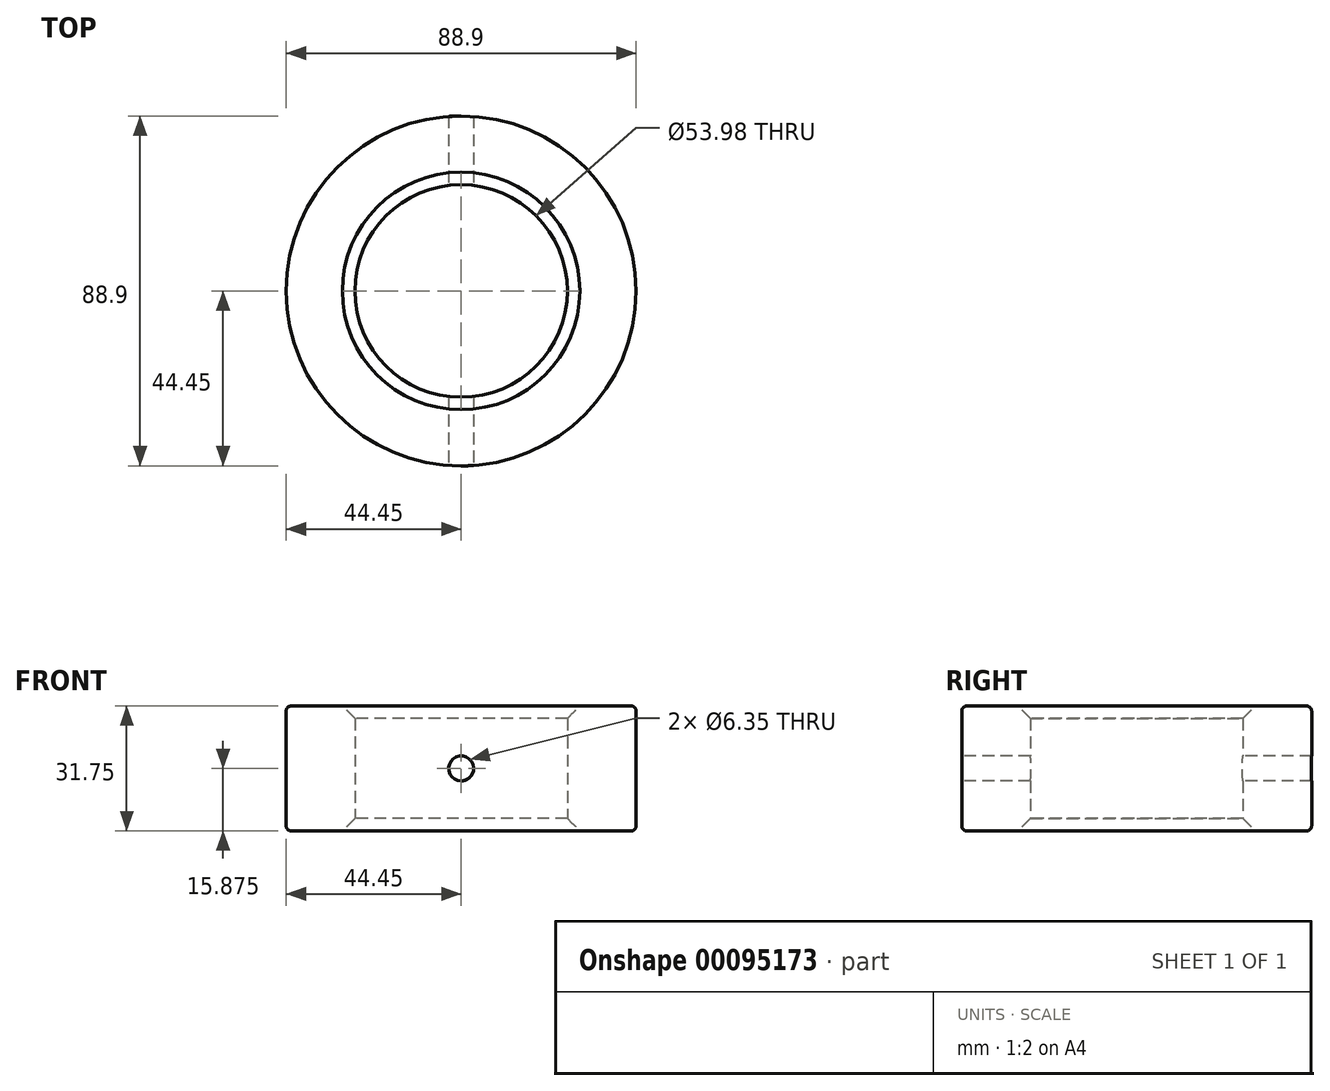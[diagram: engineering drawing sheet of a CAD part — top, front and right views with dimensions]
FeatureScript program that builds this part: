
annotation { "Feature Type Name" : "Feature", "Feature Type Description" : "" }
export const myFeature = defineFeature(function(context is Context, id is Id, definition is map)
    precondition{}
    {
        {
            var Q0;
            Q0=qCreatedBy(makeId("Top.planeOp"),FACE);
            var sketch = newSketch(context, id + "F0", { "sketchPlane" : qUnion([Q0])});
            skCircle(sketch, "E0", {"center": v(0, 0) * mm, "radius": 44.45 * mm});
            skCircle(sketch, "E1", {"center": v(0, 0) * mm, "radius": 26.99 * mm});
            skSolve(sketch);
        }
        {
            var Q0;
            Q0=makeQuery(id+"F0.imprint","IMPRINT",FACE,{"disambiguationData":[TD([[makeQuery(id+"F0.imprint","IMPRINT",EDGE,{"derivedFrom":sQuery(id+"F0.wireOp",EDGE,"E0")}),1.0]])]});
            extrude(context, id + "F1", {"entities" : qUnion([Q0]), "depth" : 31.75 * mm});
        }
        {
            var Q0;
            Q0=qCreatedBy(makeId("Front.planeOp"),FACE);
            var sketch = newSketch(context, id + "F2", { "sketchPlane" : qUnion([Q0])});
            skCircle(sketch, "E2", {"center": v(0, 15.88) * mm, "radius": 3.18 * mm});
            skSolve(sketch);
        }
        {
            var Q0;
            Q0=makeQuery(id+"F2.imprint","IMPRINT",FACE,{"disambiguationData":[TD([[makeQuery(id+"F2.imprint","IMPRINT",EDGE,{"derivedFrom":sQuery(id+"F2.wireOp",EDGE,"E2")}),1.0]])]});
            extrude(context, id + "F3", {"entities" : qUnion([Q0]), "operationType" : NewBodyOperationType.REMOVE, "endBound" : BoundingType.THROUGH_ALL, "oppositeDirection" : true, "depth" : 25.4 * mm, "hasSecondDirection" : true, "secondDirectionBound" : SecondDirectionBoundingType.THROUGH_ALL, "secondDirectionOppositeDirection" : false, "secondDirectionDepth" : 25.4 * mm});
        }
        {
            var Q0;
            Q0=makeQuery(id+"F1.opExtrude","CAP_EDGE",EDGE,{"disambiguationData":[OSD([sQuery(id+"F0.wireOp",EDGE,"E0")])],"isStart":false});
            var Q1;
            Q1=makeQuery(id+"F1.opExtrude","CAP_EDGE",EDGE,{"disambiguationData":[OSD([sQuery(id+"F0.wireOp",EDGE,"E0")])],"isStart":true});
            fillet(context, id + "F4", {"entities" : qUnion([Q0, Q1]), "radius" : 1.27 * mm, "tangentPropagation" : true, "allowEdgeOverflow" : false});
        }
        {
            var Q0;
            Q0=makeQuery(id+"F1.opExtrude","CAP_EDGE",EDGE,{"disambiguationData":[OSD([sQuery(id+"F0.wireOp",EDGE,"E1")])],"isStart":false});
            var Q1;
            Q1=makeQuery(id+"F1.opExtrude","CAP_EDGE",EDGE,{"disambiguationData":[OSD([sQuery(id+"F0.wireOp",EDGE,"E1")])],"isStart":true});
            chamfer(context, id + "F5", {"entities" : qUnion([Q0, Q1]), "width" : 3.17 * mm, "tangentPropagation" : true});
        }
    });
